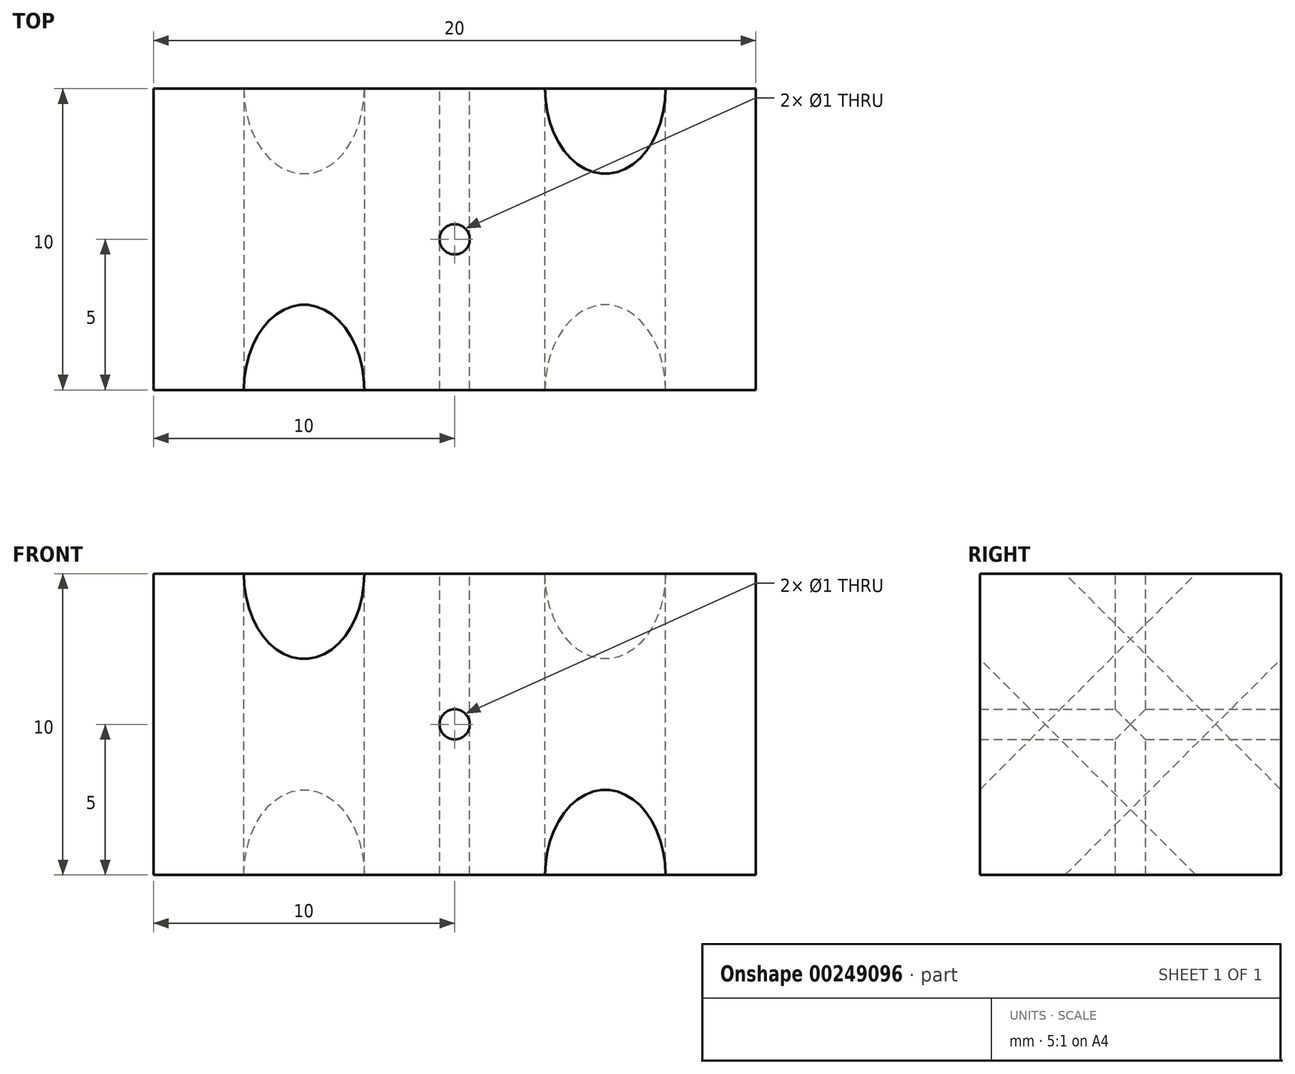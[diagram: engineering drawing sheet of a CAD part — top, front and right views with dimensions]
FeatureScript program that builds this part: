
annotation { "Feature Type Name" : "Feature", "Feature Type Description" : "" }
export const myFeature = defineFeature(function(context is Context, id is Id, definition is map)
    precondition{}
    {
        {
            var Q0;
            Q0=qCreatedBy(makeId("Right.planeOp"),FACE);
            var sketch = newSketch(context, id + "F0", { "sketchPlane" : qUnion([Q0])});
            skLineSegment(sketch, "E0.bottom", {"start": v(-5, 5) * mm, "end": v(5, 5) * mm});
            skLineSegment(sketch, "E0.top", {"start": v(-5, -5) * mm, "end": v(5, -5) * mm});
            skLineSegment(sketch, "E0.left", {"start": v(-5, 5) * mm, "end": v(-5, -5) * mm});
            skLineSegment(sketch, "E0.right", {"start": v(5, 5) * mm, "end": v(5, -5) * mm});
            skPoint(sketch, "E0.middle", {"position": v(0, 0) * mm});
            skSolve(sketch);
        }
        {
            var Q0;
            Q0=makeQuery(id+"F0.imprint","IMPRINT",FACE,{"disambiguationData":[TD([[makeQuery(id+"F0.imprint","IMPRINT",EDGE,{"derivedFrom":sQuery(id+"F0.wireOp",EDGE,"E0.bottom")}),-1.0]])]});
            extrude(context, id + "F1", {"entities" : qUnion([Q0]), "endBound" : BoundingType.SYMMETRIC, "depth" : 20 * mm});
        }
        {
            var Q0;
            Q0=makeQuery(id+"F1.opExtrude","SWEPT_EDGE",EDGE,{"disambiguationData":[OSD([sQuery(id+"F0.wireOp",EDGE,"E0.bottom"),sQuery(id+"F0.wireOp",EDGE,"E0.left")])]});
            cPlane(context, id + "F2", {"entities" : qUnion([Q0]), "cplaneType" : CPlaneType.LINE_ANGLE, "offset" : 25 * mm, "angle" : 45 * degree, "width" : 150 * mm, "height" : 150 * mm});
        }
        {
            var Q0;
            Q0=qCreatedBy(id+"F2.planeOp",FACE);
            var sketch = newSketch(context, id + "F3", { "sketchPlane" : qUnion([Q0])});
            skCircle(sketch, "E1", {"center": v(-5, 0) * mm, "radius": 2 * mm});
            skSolve(sketch);
        }
        {
            var Q0;
            Q0=makeQuery(id+"F3.imprint","IMPRINT",FACE,{"disambiguationData":[TD([[makeQuery(id+"F3.imprint","IMPRINT",EDGE,{"derivedFrom":sQuery(id+"F3.wireOp",EDGE,"E1")}),1.0]])]});
            extrude(context, id + "F4", {"entities" : qUnion([Q0]), "operationType" : NewBodyOperationType.REMOVE, "endBound" : BoundingType.THROUGH_ALL, "oppositeDirection" : true, "depth" : 25 * mm});
        }
        {
            var Q0;
            Q0=makeQuery(id+"F1.opExtrude","SWEPT_EDGE",EDGE,{"disambiguationData":[OSD([sQuery(id+"F0.wireOp",EDGE,"E0.bottom"),sQuery(id+"F0.wireOp",EDGE,"E0.right")])]});
            cPlane(context, id + "F5", {"entities" : qUnion([Q0]), "cplaneType" : CPlaneType.LINE_ANGLE, "offset" : 25 * mm, "angle" : 45 * degree, "oppositeDirection" : true, "width" : 150 * mm, "height" : 150 * mm});
        }
        {
            var Q0;
            Q0=qCreatedBy(id+"F5.planeOp",FACE);
            var sketch = newSketch(context, id + "F6", { "sketchPlane" : qUnion([Q0])});
            skCircle(sketch, "E2", {"center": v(5, 0) * mm, "radius": 2 * mm});
            skSolve(sketch);
        }
        {
            var Q0;
            Q0=makeQuery(id+"F6.imprint","IMPRINT",FACE,{"disambiguationData":[TD([[makeQuery(id+"F6.imprint","IMPRINT",EDGE,{"derivedFrom":sQuery(id+"F6.wireOp",EDGE,"E2")}),1.0]])]});
            extrude(context, id + "F7", {"entities" : qUnion([Q0]), "operationType" : NewBodyOperationType.REMOVE, "endBound" : BoundingType.THROUGH_ALL, "depth" : 25 * mm});
        }
        {
            var Q0;
            Q0=makeQuery(id+"F1.opExtrude","SWEPT_FACE",FACE,{"disambiguationData":[OSD([sQuery(id+"F0.wireOp",EDGE,"E0.right")])]});
            var sketch = newSketch(context, id + "F8", { "sketchPlane" : qUnion([Q0])});
            skCircle(sketch, "E3", {"center": v(0, 0) * mm, "radius": 0.5 * mm});
            skSolve(sketch);
        }
        {
            var Q0;
            Q0=makeQuery(id+"F8.imprint","IMPRINT",FACE,{"disambiguationData":[TD([[makeQuery(id+"F8.imprint","IMPRINT",EDGE,{"derivedFrom":sQuery(id+"F8.wireOp",EDGE,"E3")}),1.0]])]});
            extrude(context, id + "F9", {"entities" : qUnion([Q0]), "operationType" : NewBodyOperationType.REMOVE, "endBound" : BoundingType.THROUGH_ALL, "oppositeDirection" : true, "depth" : 25 * mm});
        }
        {
            var Q0;
            Q0=makeQuery(id+"F1.opExtrude","SWEPT_FACE",FACE,{"disambiguationData":[OSD([sQuery(id+"F0.wireOp",EDGE,"E0.bottom")])]});
            var sketch = newSketch(context, id + "F10", { "sketchPlane" : qUnion([Q0])});
            skCircle(sketch, "E4", {"center": v(0, 0) * mm, "radius": 0.5 * mm});
            skSolve(sketch);
        }
        {
            var Q0;
            Q0=makeQuery(id+"F10.imprint","IMPRINT",FACE,{"disambiguationData":[TD([[makeQuery(id+"F10.imprint","IMPRINT",EDGE,{"derivedFrom":sQuery(id+"F10.wireOp",EDGE,"E4")}),1.0]])]});
            extrude(context, id + "F11", {"entities" : qUnion([Q0]), "operationType" : NewBodyOperationType.REMOVE, "endBound" : BoundingType.THROUGH_ALL, "oppositeDirection" : true, "depth" : 25 * mm});
        }
    });
